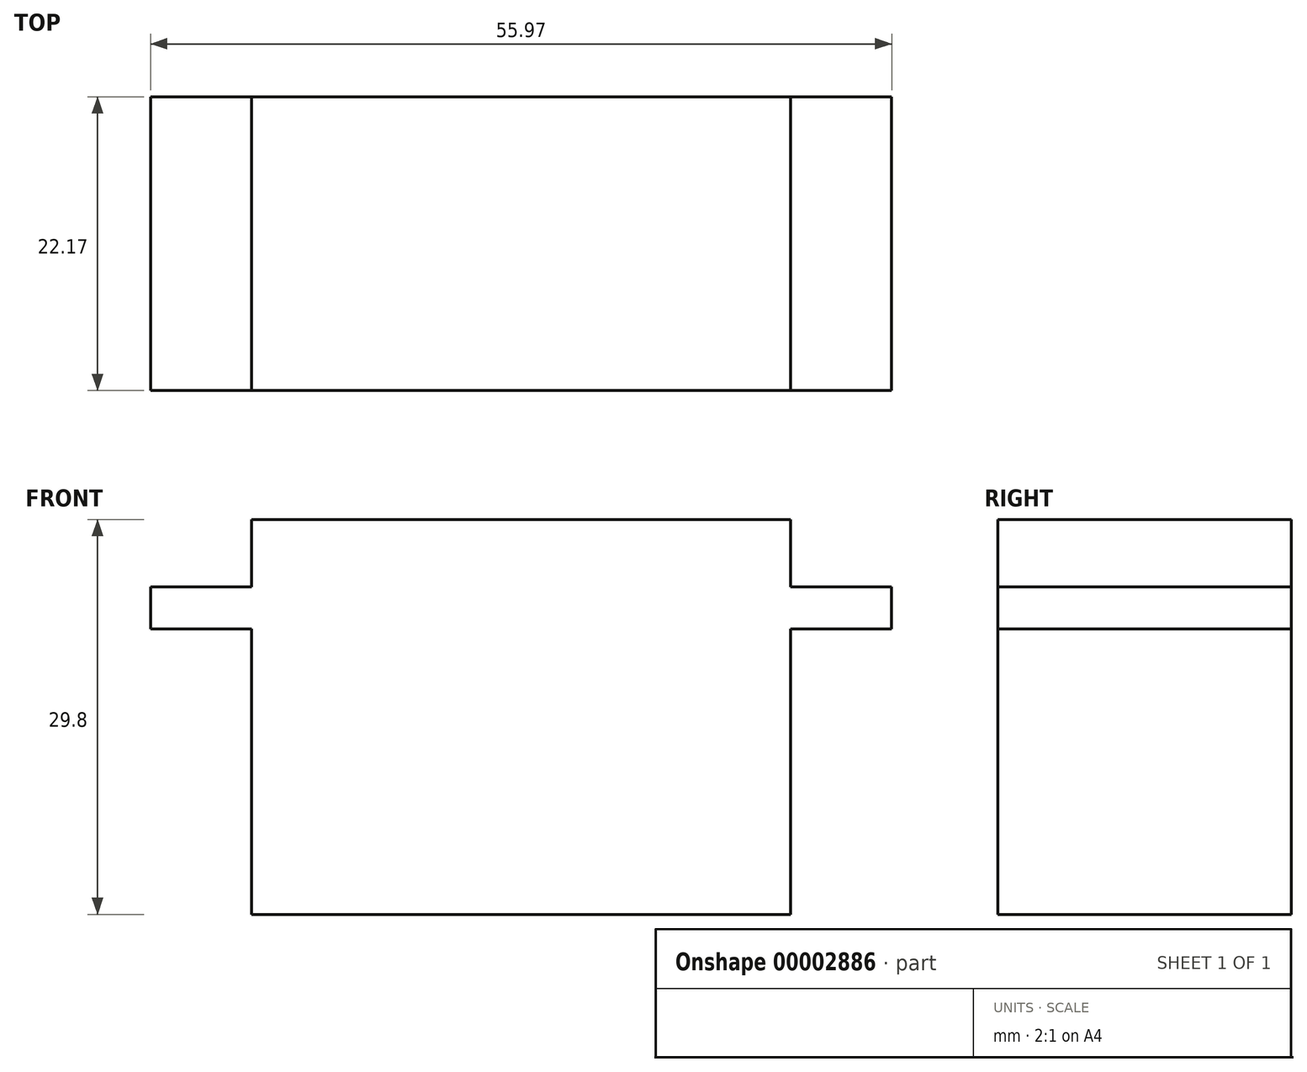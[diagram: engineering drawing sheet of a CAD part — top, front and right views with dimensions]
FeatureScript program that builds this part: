
annotation { "Feature Type Name" : "Feature", "Feature Type Description" : "" }
export const myFeature = defineFeature(function(context is Context, id is Id, definition is map)
    precondition{}
    {
        {
            var Q0;
            Q0=qCreatedBy(makeId("Top.planeOp"),FACE);
            var sketch = newSketch(context, id + "F0", { "sketchPlane" : qUnion([Q0])});
            skLineSegment(sketch, "E0.bottom", {"start": v(-18.73, 11) * mm, "end": v(22, 11) * mm});
            skLineSegment(sketch, "E0.top", {"start": v(-18.73, -11.17) * mm, "end": v(22, -11.17) * mm});
            skLineSegment(sketch, "E0.left", {"start": v(-18.73, 11) * mm, "end": v(-18.73, -11.17) * mm});
            skLineSegment(sketch, "E0.right", {"start": v(22, 11) * mm, "end": v(22, -11.17) * mm});
            skSolve(sketch);
        }
        {
            var Q0;
            Q0=makeQuery(id+"F0.imprint","IMPRINT",FACE,{"disambiguationData":[TD([[makeQuery(id+"F0.imprint","IMPRINT",EDGE,{"derivedFrom":sQuery(id+"F0.wireOp",EDGE,"E0.bottom")}),-1.0]])]});
            extrude(context, id + "F1", {"entities" : qUnion([Q0]), "depth" : 29.8 * mm});
        }
        {
            var Q0;
            Q0=makeQuery(id+"F1.opExtrude","SWEPT_FACE",FACE,{"disambiguationData":[OSD([sQuery(id+"F0.wireOp",EDGE,"E0.right")])]});
            var sketch = newSketch(context, id + "F2", { "sketchPlane" : qUnion([Q0])});
            skLineSegment(sketch, "E1.bottom", {"start": v(-11.17, 24.72) * mm, "end": v(11, 24.72) * mm});
            skLineSegment(sketch, "E1.top", {"start": v(-11.17, 21.54) * mm, "end": v(11, 21.54) * mm});
            skLineSegment(sketch, "E1.left", {"start": v(-11.17, 24.72) * mm, "end": v(-11.17, 21.54) * mm});
            skLineSegment(sketch, "E1.right", {"start": v(11, 24.72) * mm, "end": v(11, 21.54) * mm});
            skSolve(sketch);
        }
        {
            var Q0;
            Q0=makeQuery(id+"F2.imprint","IMPRINT",FACE,{"disambiguationData":[TD([[makeQuery(id+"F2.imprint","IMPRINT",EDGE,{"derivedFrom":sQuery(id+"F2.wireOp",EDGE,"E1.bottom")}),-1.0]])]});
            extrude(context, id + "F3", {"entities" : qUnion([Q0]), "operationType" : NewBodyOperationType.ADD, "depth" : 7.62 * mm});
        }
        {
            var Q0;
            Q0=makeQuery(id+"F1.opExtrude","SWEPT_FACE",FACE,{"disambiguationData":[OSD([sQuery(id+"F0.wireOp",EDGE,"E0.left")])]});
            var sketch = newSketch(context, id + "F4", { "sketchPlane" : qUnion([Q0])});
            skLineSegment(sketch, "E2.bottom", {"start": v(-11, 24.72) * mm, "end": v(11.17, 24.72) * mm});
            skLineSegment(sketch, "E2.top", {"start": v(-11, 21.54) * mm, "end": v(11.17, 21.54) * mm});
            skLineSegment(sketch, "E2.left", {"start": v(-11, 24.72) * mm, "end": v(-11, 21.54) * mm});
            skLineSegment(sketch, "E2.right", {"start": v(11.17, 24.72) * mm, "end": v(11.17, 21.54) * mm});
            skSolve(sketch);
        }
        {
            var Q0;
            Q0=makeQuery(id+"F4.imprint","IMPRINT",FACE,{"disambiguationData":[TD([[makeQuery(id+"F4.imprint","IMPRINT",EDGE,{"derivedFrom":sQuery(id+"F4.wireOp",EDGE,"E2.bottom")}),-1.0]])]});
            extrude(context, id + "F5", {"entities" : qUnion([Q0]), "operationType" : NewBodyOperationType.ADD, "depth" : 7.62 * mm});
        }
    });
